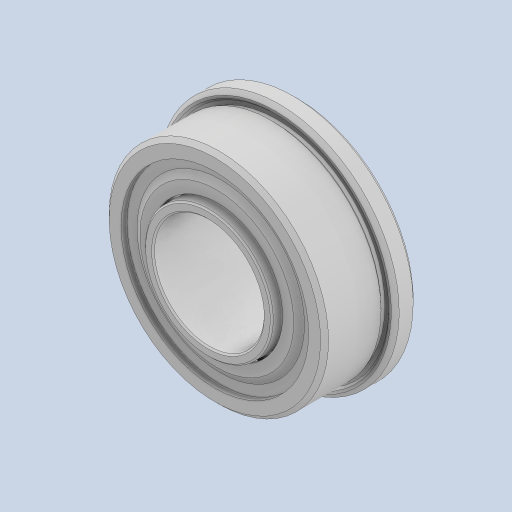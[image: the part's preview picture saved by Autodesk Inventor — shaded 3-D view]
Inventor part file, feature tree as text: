
AUTODESK INVENTOR PART (.ipt)
format: ipt  version: 2023 (Build 270158000, 158)  size: 710,144 bytes
history: native  units: in
note: dims shown in document units (in); Inventor stores cm internally (conversion verified against a paired STEP export)
features: other x13, revolve x3, fillet x1
ambient origin geometry x8: Origin, YZ Plane, XZ Plane, XY Plane, X Axis, Y Axis, Z Axis, Center Point
bodies: Solid1 (feature_tree), Solid2 (feature_tree), Solid3 (feature_tree), Solid4 (feature_tree), Solid5 (feature_tree), Solid6 (feature_tree), Solid7 (feature_tree), Solid8 (feature_tree), Solid9 (feature_tree), Solid10 (feature_tree), Solid11 (feature_tree), Solid12 (feature_tree), Solid13 (feature_tree), Solid14 (feature_tree), Solid15 (feature_tree), Solid16 (feature_tree), Solid17 (feature_tree)
feature tree (17):
  fillet  "Fillet2"  [1 undecoded]
  revolve  "Revolve3"  [1 undecoded]
  other  "CirPattern3[1]"
  other  "CirPattern3[2]"
  other  "CirPattern3[3]"
  other  "CirPattern3[4]"
  other  "CirPattern3[5]"
  other  "CirPattern3[6]"
  other  "CirPattern3[7]"
  other  "CirPattern3[8]"
  other  "CirPattern3[9]"
  other  "CirPattern3[10]"
  other  "CirPattern3[11]"
  other  "Cut-Revolve1"
  revolve  "Revolve4[1]"  [1 undecoded]
  revolve  "Revolve4[2]"  [1 undecoded]
  other  "CirPattern3[12]"
note: 4 required parameter values undecoded (feature->parameter linkage not recoverable at this tier; creation-order binding heuristic only, values carry confidence <= 0.55)
